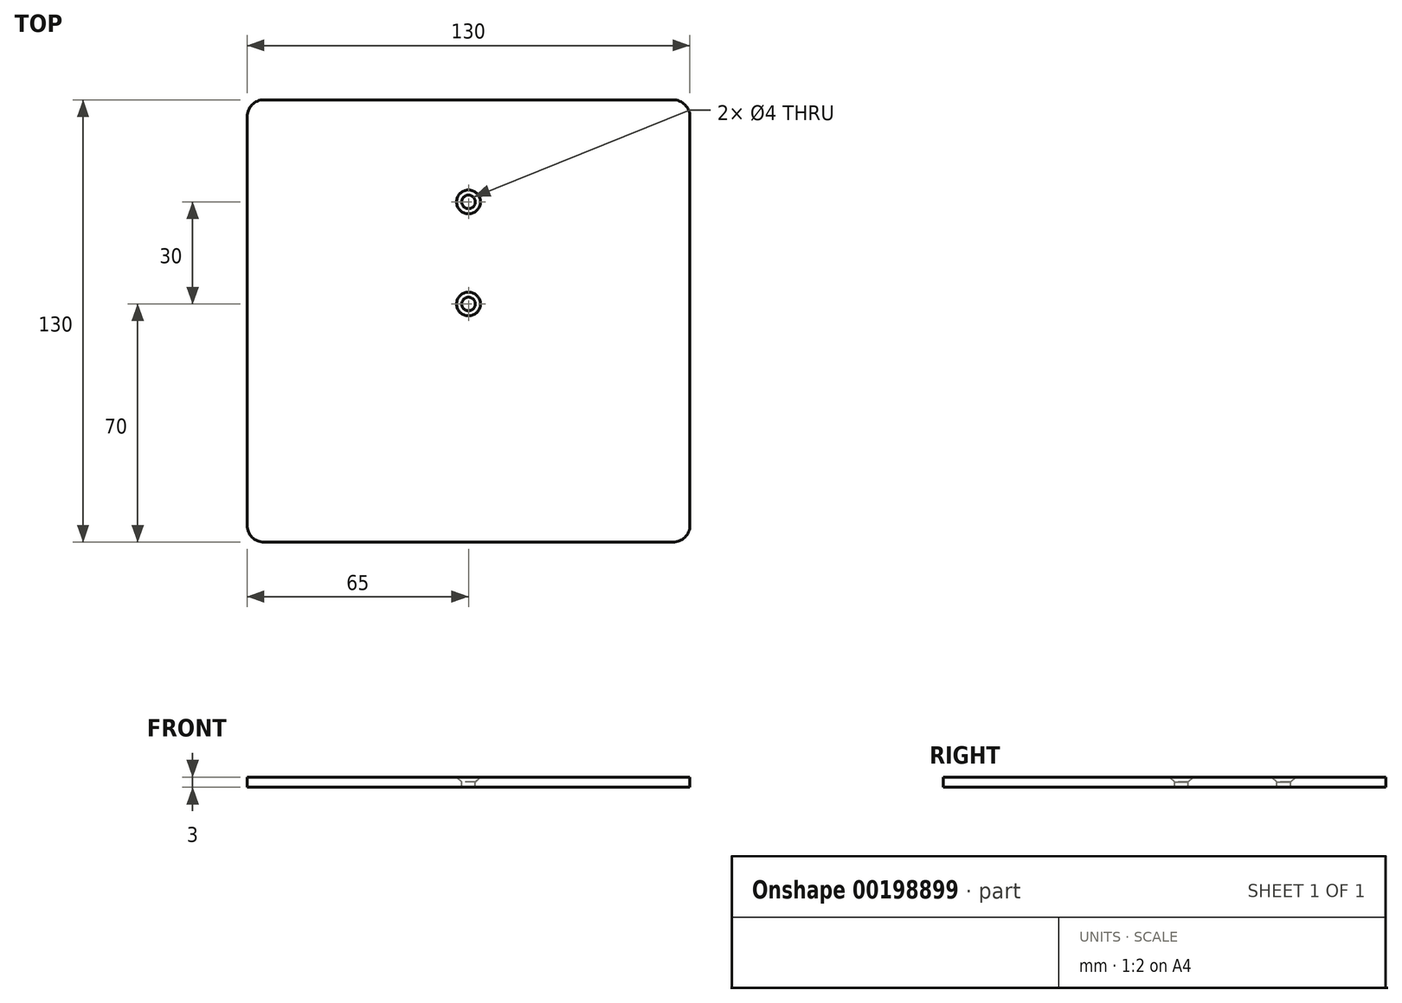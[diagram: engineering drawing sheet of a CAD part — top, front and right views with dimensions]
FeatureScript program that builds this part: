
annotation { "Feature Type Name" : "Feature", "Feature Type Description" : "" }
export const myFeature = defineFeature(function(context is Context, id is Id, definition is map)
    precondition{}
    {
        {
            var Q0;
            Q0=qCreatedBy(makeId("Top.planeOp"),FACE);
            var sketch = newSketch(context, id + "F0", { "sketchPlane" : qUnion([Q0])});
            skLineSegment(sketch, "E0.bottom", {"start": v(-65, 65) * mm, "end": v(65, 65) * mm});
            skLineSegment(sketch, "E0.top", {"start": v(-65, -65) * mm, "end": v(65, -65) * mm});
            skLineSegment(sketch, "E0.left", {"start": v(-65, 65) * mm, "end": v(-65, -65) * mm});
            skLineSegment(sketch, "E0.right", {"start": v(65, 65) * mm, "end": v(65, -65) * mm});
            skPoint(sketch, "E1", {"position": v(0, 35) * mm});
            skPoint(sketch, "E2", {"position": v(0, 5) * mm});
            skSolve(sketch);
        }
        {
            var Q0;
            Q0=makeQuery(id+"F0.imprint","IMPRINT",FACE,{"disambiguationData":[TD([[makeQuery(id+"F0.imprint","IMPRINT",EDGE,{"derivedFrom":sQuery(id+"F0.wireOp",EDGE,"E0.bottom")}),-1.0]])]});
            extrude(context, id + "F1", {"entities" : qUnion([Q0]), "oppositeDirection" : true, "depth" : 3 * mm});
        }
        {
            var Q0;
            Q0=sQuery(id+"F0.wireOp",VERTEX,"E1");
            var Q1;
            Q1=sQuery(id+"F0.wireOp",VERTEX,"E2");
            var Q2;
            Q2=makeQuery(id+"F1.opExtrude","SWEPT_BODY",BODY,{"disambiguationData":[OSD([sQuery(id+"F0.wireOp",EDGE,"E0.bottom"),sQuery(id+"F0.wireOp",EDGE,"E0.top"),sQuery(id+"F0.wireOp",EDGE,"E0.left"),sQuery(id+"F0.wireOp",EDGE,"E0.right")])]});
            hole(context, id + "F2", {"style" : HoleStyle.C_SINK, "endStyle" : HoleEndStyle.THROUGH, "holeDiameter" : 4 * mm, "cSinkDiameter" : 7 * mm, "cSinkAngle" : 90 * degree, "startFromSketch" : true, "locations" : qUnion([Q0, Q1]), "scope" : qUnion([Q2]), "isTappedThrough" : true});
        }
        {
            var Q0;
            Q0=makeQuery(id+"F1.opExtrude","SWEPT_EDGE",EDGE,{"disambiguationData":[OSD([sQuery(id+"F0.wireOp",EDGE,"E0.bottom"),sQuery(id+"F0.wireOp",EDGE,"E0.left")])]});
            var Q1;
            Q1=makeQuery(id+"F1.opExtrude","SWEPT_EDGE",EDGE,{"disambiguationData":[OSD([sQuery(id+"F0.wireOp",EDGE,"E0.bottom"),sQuery(id+"F0.wireOp",EDGE,"E0.right")])]});
            var Q2;
            Q2=makeQuery(id+"F1.opExtrude","SWEPT_EDGE",EDGE,{"disambiguationData":[OSD([sQuery(id+"F0.wireOp",EDGE,"E0.top"),sQuery(id+"F0.wireOp",EDGE,"E0.right")])]});
            var Q3;
            Q3=makeQuery(id+"F1.opExtrude","SWEPT_EDGE",EDGE,{"disambiguationData":[OSD([sQuery(id+"F0.wireOp",EDGE,"E0.top"),sQuery(id+"F0.wireOp",EDGE,"E0.left")])]});
            fillet(context, id + "F3", {"entities" : qUnion([Q0, Q1, Q2, Q3]), "radius" : 5 * mm, "tangentPropagation" : true, "allowEdgeOverflow" : false});
        }
    });
